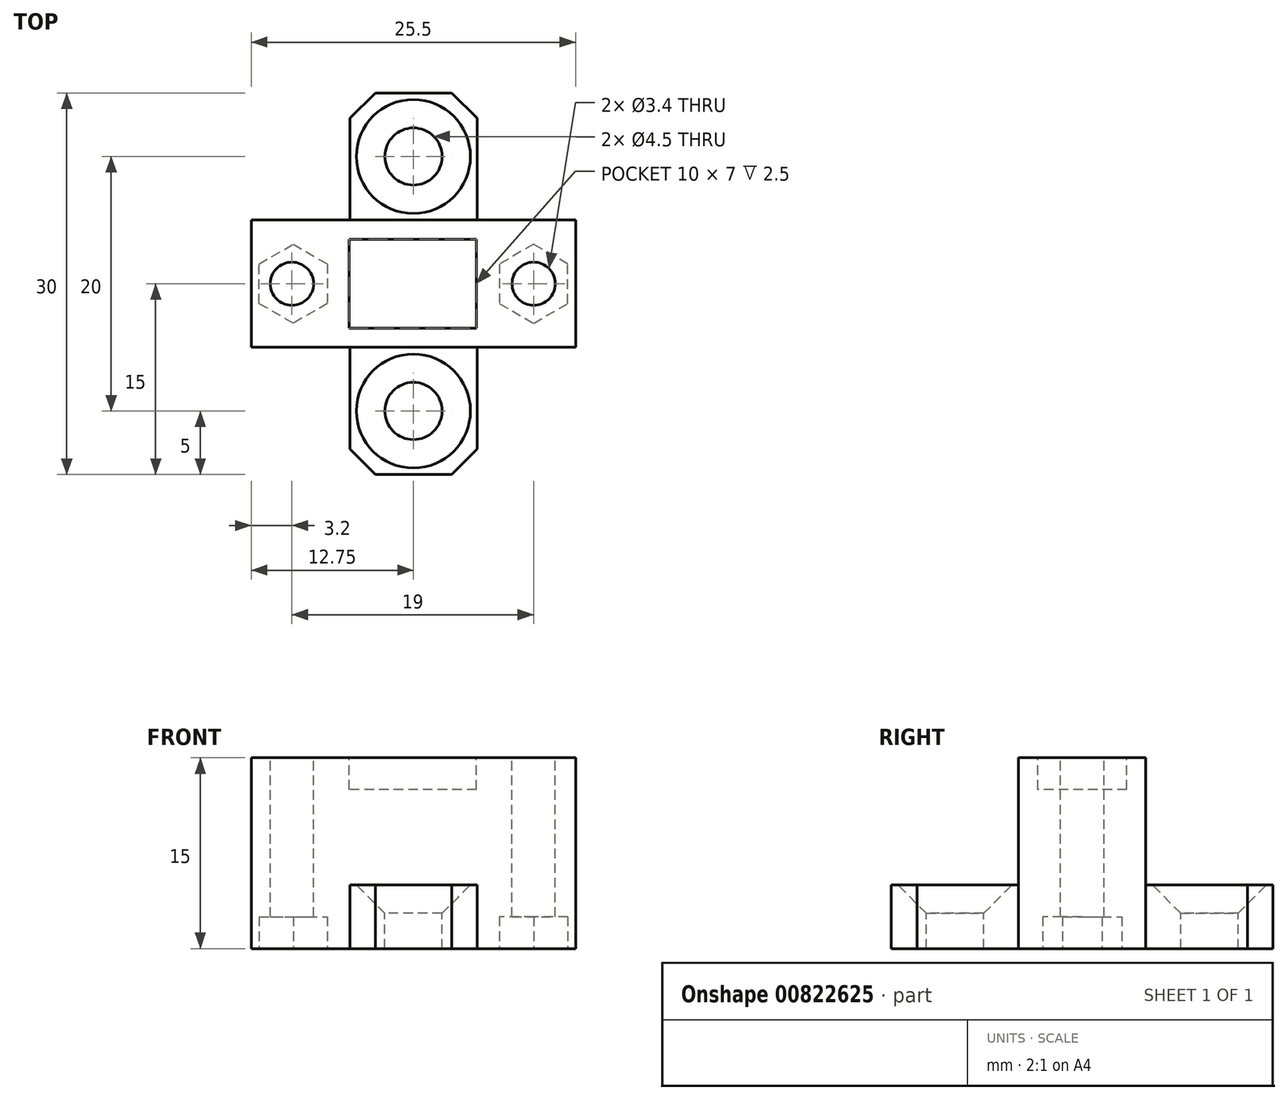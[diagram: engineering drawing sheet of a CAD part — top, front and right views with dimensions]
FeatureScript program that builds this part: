
annotation { "Feature Type Name" : "Feature", "Feature Type Description" : "" }
export const myFeature = defineFeature(function(context is Context, id is Id, definition is map)
    precondition{}
    {
        {
            var Q0;
            Q0=qCreatedBy(makeId("Top.planeOp"),FACE);
            var sketch = newSketch(context, id + "F0", { "sketchPlane" : qUnion([Q0])});
            skLineSegment(sketch, "E0.bottom", {"start": v(12.75, 5) * mm, "end": v(-12.75, 5) * mm});
            skLineSegment(sketch, "E0.top", {"start": v(12.75, -5) * mm, "end": v(-12.75, -5) * mm});
            skLineSegment(sketch, "E0.left", {"start": v(12.75, 5) * mm, "end": v(12.75, -5) * mm});
            skLineSegment(sketch, "E0.right", {"start": v(-12.75, 5) * mm, "end": v(-12.75, -5) * mm});
            skPoint(sketch, "E0.middle", {"position": v(0, 0) * mm});
            skPoint(sketch, "E1", {"position": v(-9.55, 0) * mm});
            skPoint(sketch, "E2", {"position": v(9.45, 0) * mm});
            skSolve(sketch);
        }
        {
            var Q0;
            Q0 = qSketchRegion(id + "F0", true);
            extrude(context, id + "F1", {"entities" : qUnion([Q0]), "oppositeDirection" : true, "depth" : 15 * mm, "offsetDistance" : 25 * mm});
        }
        {
            var Q0;
            Q0=sQuery(id+"F0.wireOp",VERTEX,"E1");
            var Q1;
            Q1=sQuery(id+"F0.wireOp",VERTEX,"E2");
            var Q2;
            Q2=makeQuery(id+"F1.opExtrude","SWEPT_BODY",BODY,{"disambiguationData":[OSD([sQuery(id+"F0.wireOp",EDGE,"E0.bottom"),sQuery(id+"F0.wireOp",EDGE,"E0.top"),sQuery(id+"F0.wireOp",EDGE,"E0.left"),sQuery(id+"F0.wireOp",EDGE,"E0.right")])]});
            hole(context, id + "F2", {"style" : HoleStyle.SIMPLE, "endStyle" : HoleEndStyle.THROUGH, "standardTappedOrClearance" : lookupTablePath({ "fit" : "Normal", "standard" : "ISO", "size" : "M3", "type" : "Clearance" }), "standardBlindInLast" : lookupTablePath({ "fit" : "Normal", "standard" : "ISO", "engagement" : "75%", "pitch" : "0.5 mm", "size" : "M3", "type" : "Clearance & tapped" }), "holeDiameter" : 3.4 * mm, "majorDiameter" : 5 * mm, "isTappedThrough" : true, "tappedDepth" : 3.5 * mm, "tapClearance" : 3, "startFromSketch" : true, "locations" : qUnion([Q0, Q1]), "scope" : qUnion([Q2])});
        }
        {
            var Q0;
            Q0=makeQuery(id+"F1.opExtrude","CAP_FACE",FACE,{"disambiguationData":[OSD([sQuery(id+"F0.wireOp",EDGE,"E0.bottom"),sQuery(id+"F0.wireOp",EDGE,"E0.top"),sQuery(id+"F0.wireOp",EDGE,"E0.left"),sQuery(id+"F0.wireOp",EDGE,"E0.right")])],"isStart":true});
            var sketch = newSketch(context, id + "F3", { "sketchPlane" : qUnion([Q0])});
            skLineSegment(sketch, "E3", {"start": v(9.45, 0) * mm, "end": v(-9.55, 0) * mm, "construction": true});
            skLineSegment(sketch, "E4.bottom", {"start": v(4.95, 3.5) * mm, "end": v(-5.05, 3.5) * mm});
            skLineSegment(sketch, "E4.top", {"start": v(4.95, -3.5) * mm, "end": v(-5.05, -3.5) * mm});
            skLineSegment(sketch, "E4.left", {"start": v(4.95, 3.5) * mm, "end": v(4.95, -3.5) * mm});
            skLineSegment(sketch, "E4.right", {"start": v(-5.05, 3.5) * mm, "end": v(-5.05, -3.5) * mm});
            skPoint(sketch, "E4.middle", {"position": v(-0.05, 0) * mm});
            skSolve(sketch);
        }
        {
            var Q0;
            Q0 = qSketchRegion(id + "F3", true);
            extrude(context, id + "F4", {"entities" : qUnion([Q0]), "operationType" : NewBodyOperationType.REMOVE, "oppositeDirection" : true, "depth" : 2.5 * mm, "offsetDistance" : 25 * mm});
        }
        {
            var Q0;
            Q0=makeQuery(id+"F1.opExtrude","CAP_FACE",FACE,{"disambiguationData":[OSD([sQuery(id+"F0.wireOp",EDGE,"E0.bottom"),sQuery(id+"F0.wireOp",EDGE,"E0.top"),sQuery(id+"F0.wireOp",EDGE,"E0.left"),sQuery(id+"F0.wireOp",EDGE,"E0.right")])],"isStart":false});
            var sketch = newSketch(context, id + "F5", { "sketchPlane" : qUnion([Q0])});
            skLineSegment(sketch, "E5.bottom", {"start": v(5, 5) * mm, "end": v(-5, 5) * mm});
            skLineSegment(sketch, "E5.top", {"start": v(5, 15) * mm, "end": v(-5, 15) * mm});
            skLineSegment(sketch, "E5.left", {"start": v(5, 5) * mm, "end": v(5, 15) * mm});
            skLineSegment(sketch, "E5.right", {"start": v(-5, 5) * mm, "end": v(-5, 15) * mm});
            skPoint(sketch, "E5.middle", {"position": v(0, 10) * mm});
            skLineSegment(sketch, "E6.MirrorCS", {"start": v(5, -5) * mm, "end": v(5, -15) * mm});
            skLineSegment(sketch, "E7.MirrorCS", {"start": v(5, -5) * mm, "end": v(-5, -5) * mm});
            skPoint(sketch, "E8.MirrorP", {"position": v(0, -10) * mm});
            skLineSegment(sketch, "E9.MirrorCS", {"start": v(5, -15) * mm, "end": v(-5, -15) * mm});
            skLineSegment(sketch, "E10.MirrorCS", {"start": v(-5, -5) * mm, "end": v(-5, -15) * mm});
            skSolve(sketch);
        }
        {
            var Q0;
            Q0 = qSketchRegion(id + "F5", true);
            extrude(context, id + "F6", {"entities" : qUnion([Q0]), "operationType" : NewBodyOperationType.ADD, "oppositeDirection" : true, "depth" : 5 * mm, "offsetDistance" : 25 * mm});
        }
        {
            var Q0;
            Q0=makeQuery(id+"F6.opExtrude","CAP_FACE",FACE,{"disambiguationData":[OSD([sQuery(id+"F5.wireOp",EDGE,"E5.bottom"),sQuery(id+"F5.wireOp",EDGE,"E5.top"),sQuery(id+"F5.wireOp",EDGE,"E5.left"),sQuery(id+"F5.wireOp",EDGE,"E5.right")])],"isStart":false});
            var sketch = newSketch(context, id + "F7", { "sketchPlane" : qUnion([Q0])});
            skPoint(sketch, "E11", {"position": v(0, -10) * mm});
            skPoint(sketch, "E11.positionSnap0", {"position": v(0, -15) * mm});
            skPoint(sketch, "E12.MirrorP", {"position": v(0, 10) * mm});
            skSolve(sketch);
        }
        {
            var Q0;
            Q0=sQuery(id+"F7.wireOp",VERTEX,"E11");
            var Q1;
            Q1=sQuery(id+"F7.wireOp",VERTEX,"E12.MirrorP");
            var Q2;
            Q2=makeQuery(id+"F1.opExtrude","SWEPT_BODY",BODY,{"disambiguationData":[OSD([sQuery(id+"F0.wireOp",EDGE,"E0.bottom"),sQuery(id+"F0.wireOp",EDGE,"E0.top"),sQuery(id+"F0.wireOp",EDGE,"E0.left"),sQuery(id+"F0.wireOp",EDGE,"E0.right")])]});
            hole(context, id + "F8", {"style" : HoleStyle.C_SINK, "endStyle" : HoleEndStyle.THROUGH, "standardTappedOrClearance" : lookupTablePath({ "fit" : "Normal", "standard" : "ISO", "size" : "M4", "type" : "Clearance" }), "standardBlindInLast" : lookupTablePath({ "fit" : "Normal", "standard" : "ISO", "engagement" : "75%", "pitch" : "0.7 mm", "size" : "M4", "type" : "Clearance & tapped" }), "holeDiameter" : 4.5 * mm, "cSinkDiameter" : 8.96 * mm, "cSinkAngle" : 90 * degree, "majorDiameter" : 5 * mm, "isTappedThrough" : true, "tappedDepth" : 3.5 * mm, "tapClearance" : 3, "startFromSketch" : true, "locations" : qUnion([Q0, Q1]), "scope" : qUnion([Q2])});
        }
        {
            var Q0;
            Q0=makeQuery(id+"F6.opExtrude","SWEPT_EDGE",EDGE,{"disambiguationData":[OSD([sQuery(id+"F5.wireOp",EDGE,"E9.MirrorCS"),sQuery(id+"F5.wireOp",EDGE,"E10.MirrorCS")])]});
            var Q1;
            Q1=makeQuery(id+"F6.opExtrude","SWEPT_EDGE",EDGE,{"disambiguationData":[OSD([sQuery(id+"F5.wireOp",EDGE,"E6.MirrorCS"),sQuery(id+"F5.wireOp",EDGE,"E9.MirrorCS")])]});
            var Q2;
            Q2=makeQuery(id+"F6.opExtrude","SWEPT_EDGE",EDGE,{"disambiguationData":[OSD([sQuery(id+"F0.wireOp",EDGE,"E0.bottom"),sQuery(id+"F5.wireOp",EDGE,"E6.MirrorCS"),sQuery(id+"F5.wireOp",EDGE,"E7.MirrorCS")])]});
            var Q3;
            Q3=makeQuery(id+"F6.opExtrude","SWEPT_EDGE",EDGE,{"disambiguationData":[OSD([sQuery(id+"F0.wireOp",EDGE,"E0.bottom"),sQuery(id+"F5.wireOp",EDGE,"E7.MirrorCS"),sQuery(id+"F5.wireOp",EDGE,"E10.MirrorCS")])]});
            var Q4;
            Q4=makeQuery(id+"F6.opExtrude","SWEPT_EDGE",EDGE,{"disambiguationData":[OSD([sQuery(id+"F0.wireOp",EDGE,"E0.top"),sQuery(id+"F5.wireOp",EDGE,"E5.bottom"),sQuery(id+"F5.wireOp",EDGE,"E5.left")])]});
            var Q5;
            Q5=makeQuery(id+"F6.opExtrude","SWEPT_EDGE",EDGE,{"disambiguationData":[OSD([sQuery(id+"F5.wireOp",EDGE,"E5.top"),sQuery(id+"F5.wireOp",EDGE,"E5.left")])]});
            var Q6;
            Q6=makeQuery(id+"F6.opExtrude","SWEPT_EDGE",EDGE,{"disambiguationData":[OSD([sQuery(id+"F5.wireOp",EDGE,"E5.top"),sQuery(id+"F5.wireOp",EDGE,"E5.right")])]});
            chamfer(context, id + "F9", {"entities" : qUnion([Q0, Q1, Q2, Q3, Q4, Q5, Q6]), "width" : 2 * mm, "tangentPropagation" : true});
        }
        {
            var Q0;
            Q0=makeQuery(id+"F6.boolean.opBoolean","MERGE",FACE,{"derivedFrom":[makeQuery(id+"F1.opExtrude","CAP_FACE",FACE,{"disambiguationData":[OSD([sQuery(id+"F0.wireOp",EDGE,"E0.bottom"),sQuery(id+"F0.wireOp",EDGE,"E0.top"),sQuery(id+"F0.wireOp",EDGE,"E0.left"),sQuery(id+"F0.wireOp",EDGE,"E0.right")])],"isStart":false}),makeQuery(id+"F6.opExtrude","CAP_FACE",FACE,{"disambiguationData":[OSD([sQuery(id+"F5.wireOp",EDGE,"E5.bottom"),sQuery(id+"F5.wireOp",EDGE,"E5.top"),sQuery(id+"F5.wireOp",EDGE,"E5.left"),sQuery(id+"F5.wireOp",EDGE,"E5.right")])],"isStart":true}),makeQuery(id+"F6.opExtrude","CAP_FACE",FACE,{"disambiguationData":[OSD([sQuery(id+"F5.wireOp",EDGE,"E6.MirrorCS"),sQuery(id+"F5.wireOp",EDGE,"E7.MirrorCS"),sQuery(id+"F5.wireOp",EDGE,"E9.MirrorCS"),sQuery(id+"F5.wireOp",EDGE,"E10.MirrorCS")])],"isStart":true})]});
            var sketch = newSketch(context, id + "F10", { "sketchPlane" : qUnion([Q0])});
            skCircle(sketch, "E13.cCircle", {"center": v(9.45, 0) * mm, "radius": 2.68 * mm, "construction": true});
            skLineSegment(sketch, "E13.0", {"start": v(9.45, -3.1) * mm, "end": v(6.77, -1.55) * mm});
            skLineSegment(sketch, "E13.1", {"start": v(6.77, -1.55) * mm, "end": v(6.77, 1.55) * mm});
            skLineSegment(sketch, "E13.2", {"start": v(6.77, 1.55) * mm, "end": v(9.45, 3.1) * mm});
            skLineSegment(sketch, "E13.3", {"start": v(9.45, 3.1) * mm, "end": v(12.13, 1.55) * mm});
            skLineSegment(sketch, "E13.4", {"start": v(12.13, 1.55) * mm, "end": v(12.13, -1.55) * mm});
            skLineSegment(sketch, "E13.5", {"start": v(12.13, -1.55) * mm, "end": v(9.45, -3.1) * mm});
            skPoint(sketch, "E13.0.midPoint", {"position": v(8.1, -2.32) * mm});
            skCircle(sketch, "E14.MirrorC", {"center": v(-9.45, 0) * mm, "radius": 2.68 * mm, "construction": true});
            skPoint(sketch, "E15.MirrorP", {"position": v(-8.1, -2.32) * mm});
            skLineSegment(sketch, "E16.MirrorCS", {"start": v(-9.45, -3.1) * mm, "end": v(-6.77, -1.55) * mm});
            skLineSegment(sketch, "E17.MirrorCS", {"start": v(-12.13, -1.55) * mm, "end": v(-9.45, -3.1) * mm});
            skLineSegment(sketch, "E18.MirrorCS", {"start": v(-6.77, -1.55) * mm, "end": v(-6.77, 1.55) * mm});
            skLineSegment(sketch, "E19.MirrorCS", {"start": v(-9.45, 3.1) * mm, "end": v(-12.13, 1.55) * mm});
            skLineSegment(sketch, "E20.MirrorCS", {"start": v(-12.13, 1.55) * mm, "end": v(-12.13, -1.55) * mm});
            skLineSegment(sketch, "E21.MirrorCS", {"start": v(-6.77, 1.55) * mm, "end": v(-9.45, 3.1) * mm});
            skSolve(sketch);
        }
        {
            var Q0;
            Q0 = qSketchRegion(id + "F10", true);
            extrude(context, id + "F11", {"entities" : qUnion([Q0]), "operationType" : NewBodyOperationType.REMOVE, "oppositeDirection" : true, "depth" : 2.5 * mm, "offsetDistance" : 25 * mm});
        }
    });
